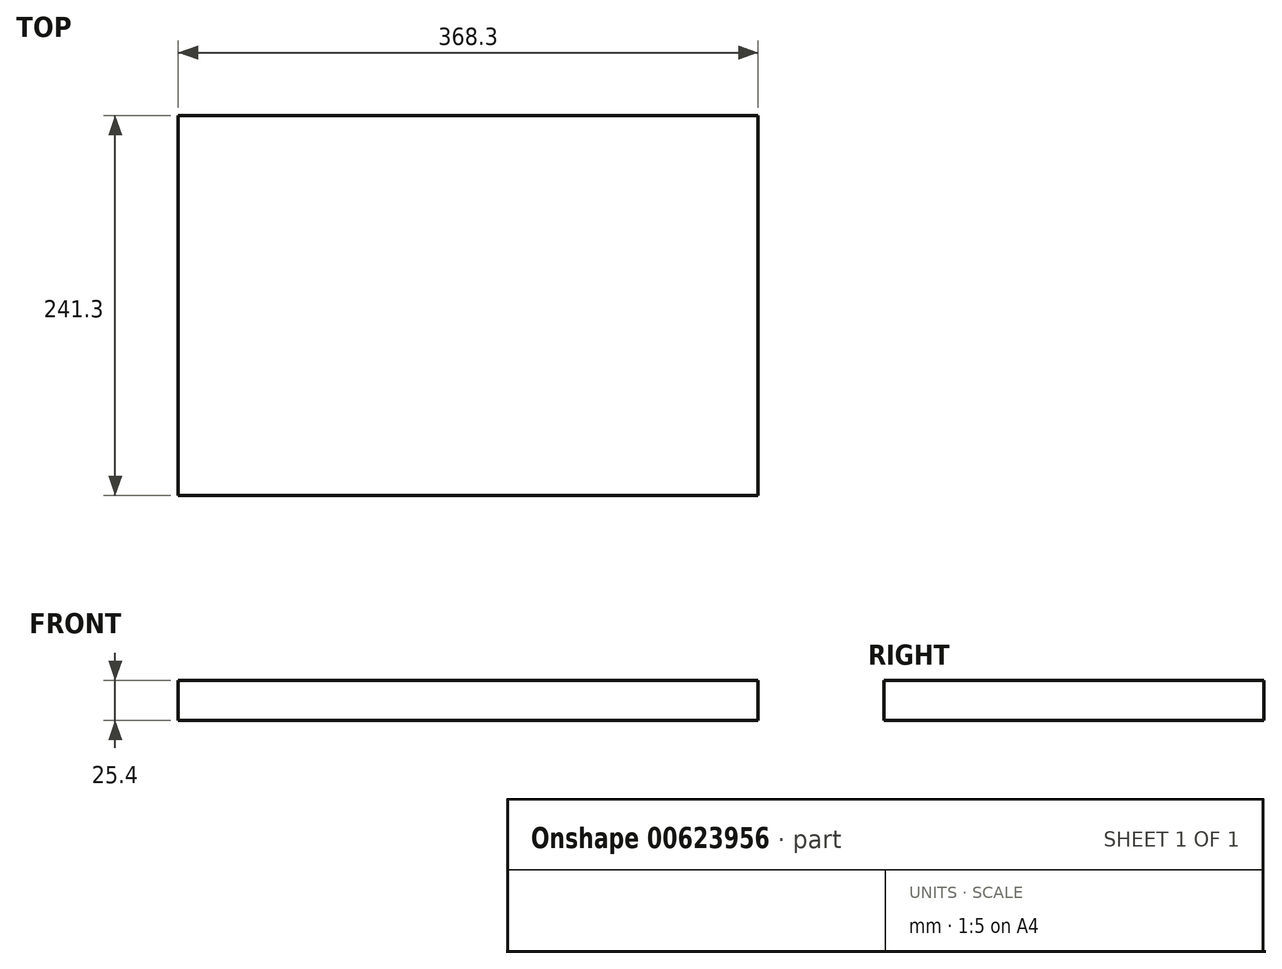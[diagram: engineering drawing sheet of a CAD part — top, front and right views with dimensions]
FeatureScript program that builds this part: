
annotation { "Feature Type Name" : "Feature", "Feature Type Description" : "" }
export const myFeature = defineFeature(function(context is Context, id is Id, definition is map)
    precondition{}
    {
        {
            var Q0;
            Q0=qCreatedBy(makeId("Top.planeOp"),FACE);
            var sketch = newSketch(context, id + "F0", { "sketchPlane" : qUnion([Q0])});
            skLineSegment(sketch, "E0.bottom", {"start": v(-179.1, 119) * mm, "end": v(189.2, 119) * mm});
            skLineSegment(sketch, "E0.top", {"start": v(-179.1, -122.3) * mm, "end": v(189.2, -122.3) * mm});
            skLineSegment(sketch, "E0.left", {"start": v(-179.1, 119) * mm, "end": v(-179.1, -122.3) * mm});
            skLineSegment(sketch, "E0.right", {"start": v(189.2, 119) * mm, "end": v(189.2, -122.3) * mm});
            skSolve(sketch);
        }
        {
            var Q0;
            Q0=makeQuery(id+"F0.imprint","IMPRINT",FACE,{"disambiguationData":[TD([[makeQuery(id+"F0.imprint","IMPRINT",EDGE,{"derivedFrom":sQuery(id+"F0.wireOp",EDGE,"E0.bottom")}),-1.0]])]});
            extrude(context, id + "F1", {"entities" : qUnion([Q0]), "depth" : 25.4 * mm, "offsetDistance" : 25.4 * mm});
        }
    });
